# Revit family: 93602219(2023)
name_source: partatom
category: Plumbing Fixtures
units: mm (PartAtom-declared; Revit-internal decimal feet)

## family parameters
Always vertical = Yes
Cut with Voids When Loaded = No
OmniClass Number = 23.45.55.00
OmniClass Title = Sanitary Faucets, Wastes
Part Type = Normal
Room Calculation Point = No
Round Connector Dimension = Use Diameter
Shared = No
Work Plane-Based = No

## types (1)
- 93602219 Washbasin faucet, 3 V, Bluetooth
    2D/3D/BIM Files URL = http://static.hansa.com
    Advanced Features = 3S-installation system for safe and simple mounting
    Aerator = PCA® - constant flow rate regardless of pressure variations;Adjustable flow angle
    Afterflow Period = 3 s (1-20 s)
    AssetType = Fixed
    Automatic Flush Frequency = off (off/1-120 h)
    Automatic Flush Period = 30 s (1-1800 s)
    BIMObjectName = 93602219(2023)
    Backflow Prevention EN1717 = AA
    Battery = AA 1.5 V Lithium x 2
    Bluetooth = 5.x (D060576)
    BodyMaterial = Brass
    Brand = HANSA
    CO2 Emissions (A1-A3) = 12.6
    CO2 Emissions (A4) = 0.46
    CO2 Emissions (B7) = 430
    CO2 Emissions (C1) = 0
    CO2 Emissions (C2) = 0.02
    CO2 Emissions (C3) = 0.03
    CO2 Emissions (C4) = 0.35
    CO2 Emissions (D) = -9.2
    Catalog Drawing URL = http://static.hansa.com
    CloseOffRating = 0
    Color = Chrome
    Connection = Flexible inlet pipes
    Connection Size = G3/8
    Default Elevation = 0 mm  [stored 0 ft]
    Dimension Drawing URL = http://static.hansa.com
    DurationUnit = Year
    EAN Number = 4057304019555
    EMC Directive = 2014/53/EU , 2011/65/EU
    EN Standard = EN 15091
    ETIM Class Number = EC010340 Electronic tap
    Electrical Connection = 9 V
    Electronic Parts = ;Light indicated function(s);Low battery indicator
    FDV Document URL = http://www.hansa.com
    FaucetMainMaterial = Brass
    Features = Touchless;Battery-operated;External transformer;Bluetooth®
    Finish = Polished
    Flow Drawing URL = http://static.hansa.com
    Flow Rate At 300kPa With Flow Controller = 0.1 L/s
    FlowCoefficient = 0
    Group = Washbasin faucet
    IfcExportAs = IfcValveType
    IfcExportType = FAUCET
    InletConnectionSize = 10 mm  [stored 0.0328084 ft]
    Installation Type = Deck mounted
    Lever Handle = Temperature control handle
    Long Marketing = Electra 93 series give you a clean classic design with beautiful round body flowing into round spout design with a clear design line framing the faucet design.
A Classic design with improved height for any installation.

Key Features
Aerator with Tilt function +/- 10° for more flexible installation
Newest Sensor technology for better detection and operation comfort
Bluetooth technology for easy adjustment to personalize settings 
Antiscalding protection
Temperature measurement
Battery and power cable
    Manufacturer = HANSA
    ManufacturerName = HANSA
    ManufacturerURL = http://www.hansa.com
    Market = International;Finland;Germany;Austria;Switzerland;Belgium;Netherlands;Italy
    Material = Brass
    Max Flow Period = 2 min (1 - 1800 s)
    Max. Hot Water Supply = 70 °C
    Mechanical Parts = Mixing valve for manual temperature control;Non-return valve(s);Litter filter(s)
    Mobile Product Information URL = http://mpi.hansa.com
    Model = 93602219 Washbasin faucet, 3 V, Bluetooth
    ModelReference = 93602219
    Mounting Holes = 1 hole
    NBSDescription = Water supply fittings for wash basins and troughs
    NBSReference = 45-35-70/371
    Name = 93602219 Washbasin faucet, 3 V, Bluetooth
    Name_en = 93602219 Washbasin faucet, 3 V, Bluetooth
    Noise Class = I (ISO 3822)
    NominalDepth = 168 mm  [stored 0.551181 ft]
    NominalHeight = 190 mm  [stored 0.62336 ft]
    NominalWidth = 69 mm
    Operating Distance = 20-130 mm (110/130/160 mm)
    Operating Voltage = 39 V
    Product Code = 93602219
    Product Family = HANSAELECTRA Safety
    Product Image URL = http://static.hansa.com
    Product URL = http://static.hansa.com
    Protection Class = IP 55
    Sales Package dimensions (LxWxH) = 568 x 182 x 78
    Shape = Sculptured
    Size = 70x170x190 mm
    Spout Projection = 124 mm
    Spout Type = Fixed spout
    Surface treatment = Chrome
    Technical DataSheet URL = http://www.hansa.com
    Temperature Adjustments = Adjustable hot water stop (included, retrofittable)
    UNSPSC Class Number = 30181700 Faucets or taps
    URL Declaration Of Performance (DOP) = http://static.hansa.com
    URL Declaration of Asbestos = http://static.hansa.com
    URL Declaration of Conformity = http://static.hansa.com
    URL Declaration of SCIP = http://static.hansa.com
    URL EU Packaging Declaration = http://static.hansa.com
    URL EcoLabel Declaration = http://static.hansa.com
    URL Materials Declaration = http://www.hansa.com
    URL REACH = http://static.hansa.com
    URL UWL = http://static.hansa.com
    URL WEEE = http://static.hansa.com
    Uniclass2 = Pr_40_30_96_96
    Uniclass2015Description = Washbasin manual water supply sets
    Uniclass2015Reference = Pr_40_20_87_96
    Version = 1
    VersionDate = 01/06/2023
    Warranty Information URL = http://warranty.hansa.com
    WarrantyDescription = http://warranty.hansa.com
    WarrantyDurationUnit = Year
    Working Pressure = 100 - 1000 kPa

note: [stored X ft] marks values corroborated as IEEE doubles in the binary element streams (Revit-internal decimal feet)

## geometry (parser evidence)
native form markers: Sweep x7
no freeform markers — native parametric forms only
